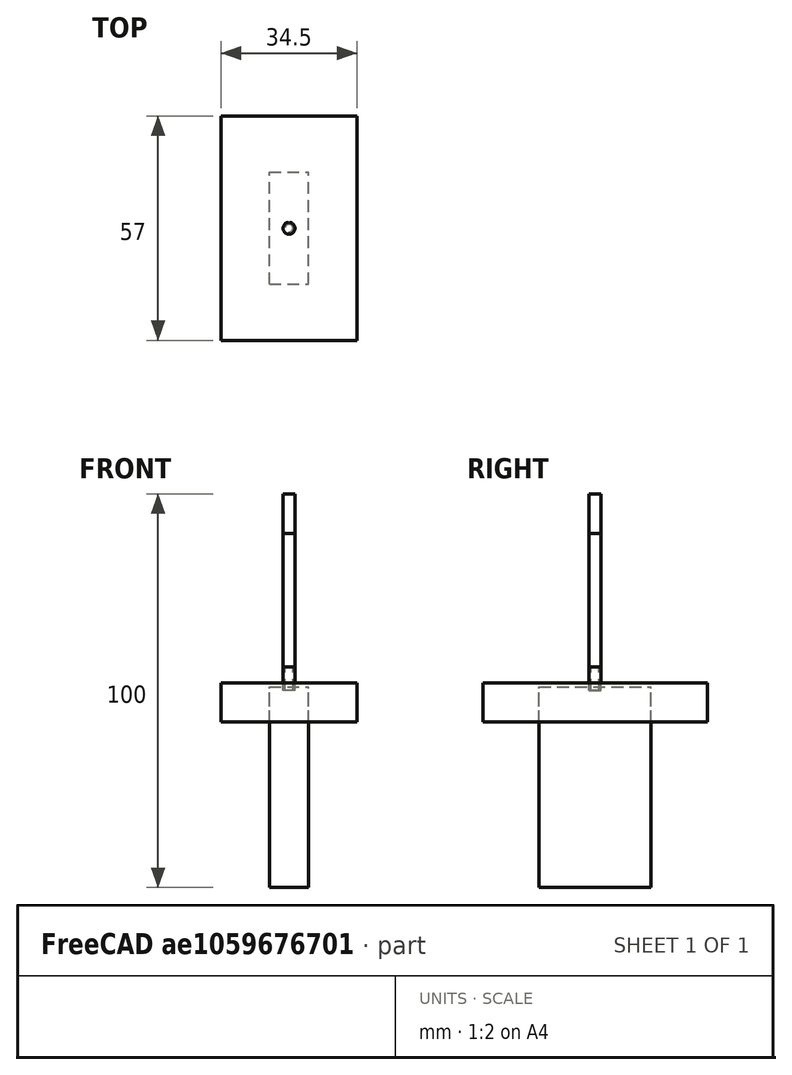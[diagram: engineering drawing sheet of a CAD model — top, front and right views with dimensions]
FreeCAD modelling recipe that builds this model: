
FCSTD DOCUMENT  (FreeCAD 1.0R39109 (Git))
Label: BackFastening_1
License: All rights reserved
LicenseURL: http://en.wikipedia.org/wiki/All_rights_reserved
objects: Path::FeaturePython×15, Part::FeaturePython×11, App::DocumentObjectGroup×9, App::FeaturePython×3, Part::Feature×1
note: 16 computed .brp shape members not serialized (recipe doc carries the construction recipe); baked Part::Feature solids carry a one-line shape summary decoded from their .brp

FEATURE [Part::Feature] Solid  label="PlateFastnest_1"
  shape: bbox 49 x 26.5 x 8 mm, 26 faces (baked)
FEATURE [App::FeaturePython] SetupSheet  # Path/CAM operation (typed FeaturePython)
  ClearanceHeightExpression = OpStockZMax+SetupSheet.ClearanceHeightOffset
  ClearanceHeightOffset = 5
  CoolantMode = 0
  CoolantModes = None | Flood | Mist
  FinalDepthExpression = OpFinalDepth
  HorizRapid = 0
  SafeHeightExpression = OpStockZMax+SetupSheet.SafeHeightOffset
  SafeHeightOffset = 3
  StartDepthExpression = OpStartDepth
  StepDownExpression = OpToolDiameter
  VertRapid = 0
FEATURE [Part::FeaturePython] Clone  label="Model-PlateFastnest_1"  # Draft clone (typed FeaturePython)
  AttacherType = Attacher::AttachEngine3D
  Fuse = false
  Objects = -> [Solid]
  PathResource = Model
  Placement = pos=(-13.25,-24.5,-8) rot=(0,0,-1;4.71239rad)
  Scale = (1,1,1)
FEATURE [App::DocumentObjectGroup] Model
  Group = -> [Clone]
FEATURE [Part::FeaturePython] Stock001  # WARN: FeaturePython — macro-defined, semantics opaque (R4)
  Base = -> Model
  ExtXneg = 4
  ExtXpos = 4
  ExtYneg = 4
  ExtYpos = 4
  ExtZneg = 0
  ExtZpos = 2
  Placement = pos=(-13.25,-24.5,-8) rot=(0,0,1;0rad)
  StockType = FromBase
FEATURE [Part::FeaturePython] ToolBit001  label="3mm Endmill"  # Path/CAM toolbit (typed FeaturePython)
  BitPropertyNames = Chipload | CuttingEdgeHeight | Diameter | Flutes | Length | Material | ShankDiameter | SpindleDirection
  BitShape = <path>
  Chipload = 0
  CuttingEdgeHeight = 15
  Diameter = 3
  File = <path>
  Flutes = 0
  Length = 50
  Material = 0
  ShankDiameter = 3
  ShapeName = endmill
  SpindleDirection = 0
FEATURE [Path::FeaturePython] _mm_Endmill  label="3mm Endmill001"  # Path/CAM operation (typed FeaturePython)
  HorizFeed = 6.66667
  HorizRapid = 0
  SpindleDir = 0
  SpindleSpeed = 10000
  Tool = -> ToolBit001
  ToolNumber = 2
  VertFeed = 6.66667
  VertRapid = 0
  expr: HorizRapid = SetupSheet.HorizRapid
  expr: VertRapid = SetupSheet.VertRapid
FEATURE [App::DocumentObjectGroup] Tools
  Group = -> [_mm_Endmill]
FEATURE [Path::FeaturePython] Adaptive  label="FaceMill"  # Path/CAM operation (typed FeaturePython)
  Active = true
  Base = -> [Clone]
  ClearanceHeight = 7
  CoolantMode = 0
  CycleTime = 00:08:12
  ExtensionCorners = true
  ExtensionFeature = -> [Clone]
  ExtensionLengthDefault = 1.5
  FinalDepth = 0
  FinishDepth = 0
  FinishingProfile = true
  ForceInsideOut = false
  HelixAngle = 5
  HelixConeAngle = 0
  HelixDiameterLimit = 0
  KeepToolDownRatio = 3
  LiftDistance = 0
  OpFinalDepth = 0
  OpStartDepth = 2
  OpStockZMax = 2
  OpStockZMin = -8
  OpToolDiameter = 3
  OperationType = 0
  SafeHeight = 5
  Side = 1
  StartDepth = 2
  StepDown = 3
  StepOver = 20
  StockToLeave = 0
  StopProcessing = false
  Stopped = false
  Tolerance = 0.09
  ToolController = -> _mm_Endmill
  UseHelixArcs = false
  UseOutline = false
  expr: ClearanceHeight = OpStockZMax + SetupSheet.ClearanceHeightOffset
  expr: ExtensionLengthDefault = OpToolDiameter / 2
  expr: FinalDepth = OpFinalDepth
  expr: SafeHeight = OpStockZMax + SetupSheet.SafeHeightOffset
  expr: StartDepth = OpStartDepth
  expr: StepDown = OpToolDiameter
FEATURE [Path::FeaturePython] Adaptive001  label="OutCut"  # Path/CAM operation (typed FeaturePython)
  Active = true
  Base = -> [Clone]
  ClearanceHeight = 7
  CoolantMode = 0
  CycleTime = 00:11:38
  ExtensionCorners = true
  ExtensionLengthDefault = 1.5
  FinalDepth = -8
  FinishDepth = 0
  FinishingProfile = true
  ForceInsideOut = false
  HelixAngle = 5
  HelixConeAngle = 0
  HelixDiameterLimit = 1
  KeepToolDownRatio = 3
  LiftDistance = 0
  OpFinalDepth = -8
  OpStartDepth = 2
  OpStockZMax = 2
  OpStockZMin = -8
  OpToolDiameter = 3
  OperationType = 1
  SafeHeight = 5
  Side = 0
  StartDepth = 2
  StepDown = 6
  StepOver = 20
  StockToLeave = 0
  StopProcessing = false
  Stopped = false
  Tolerance = 0.1
  ToolController = -> _mm_Endmill
  UseHelixArcs = false
  UseOutline = false
  expr: ClearanceHeight = OpStockZMax + SetupSheet.ClearanceHeightOffset
  expr: ExtensionLengthDefault = OpToolDiameter / 2
  expr: FinalDepth = OpFinalDepth
  expr: SafeHeight = OpStockZMax + SetupSheet.SafeHeightOffset
  expr: StartDepth = OpStartDepth
  expr: StepDown = OpToolDiameter * 2
FEATURE [App::DocumentObjectGroup] Operations
  Group = -> [Adaptive,Adaptive001]
FEATURE [Path::FeaturePython] Job  label="OutCut001"  # Path/CAM operation (typed FeaturePython)
  CycleTime = 00:19:50
  Fixtures = G54
  GeometryTolerance = 0.01
  JobType = 0
  Model = -> Model
  Operations = -> Operations
  OrderOutputBy = 0
  PostProcessor = 11
  PostProcessorArgs = --bcnc
  PostProcessorOutputFile = %D\%d_OutCut
  SetupSheet = -> SetupSheet
  SplitOutput = false
  Stock = -> Stock001
  Tools = -> Tools
FEATURE [App::FeaturePython] SetupSheet001  # Path/CAM operation (typed FeaturePython)
  ClearanceHeightExpression = OpStockZMax+SetupSheet001.ClearanceHeightOffset
  ClearanceHeightOffset = 5
  CoolantMode = 0
  CoolantModes = None | Flood | Mist
  FinalDepthExpression = OpFinalDepth
  HorizRapid = 0
  SafeHeightExpression = OpStockZMax+SetupSheet001.SafeHeightOffset
  SafeHeightOffset = 3
  StartDepthExpression = OpStartDepth
  StepDownExpression = OpToolDiameter
  VertRapid = 0
FEATURE [Part::FeaturePython] Clone001  label="Model-Model-PlateFastnest_1"  # Draft clone (typed FeaturePython)
  AttacherType = Attacher::AttachEngine3D
  Fuse = false
  Objects = -> [Clone]
  PathResource = Model
  Placement = pos=(-4,-13.25,-49) rot=(-0.707107,0,-0.707107;3.14159rad)
  Scale = (1,1,1)
FEATURE [App::DocumentObjectGroup] Model001
  Group = -> [Clone001]
FEATURE [Part::FeaturePython] ToolBit002  label="3mm Endmill002"  # Path/CAM toolbit (typed FeaturePython)
  BitPropertyNames = Chipload | CuttingEdgeHeight | Diameter | Flutes | Length | Material | ShankDiameter | SpindleDirection
  BitShape = <path>
  Chipload = 0
  CuttingEdgeHeight = 15
  Diameter = 3
  File = <path>
  Flutes = 0
  Length = 50
  Material = 0
  ShankDiameter = 3
  ShapeName = endmill
  SpindleDirection = 0
FEATURE [Path::FeaturePython] _mm_Endmill002  label="3mm Endmill003"  # Path/CAM operation (typed FeaturePython)
  HorizFeed = 3.33333
  HorizRapid = 0
  SpindleDir = 0
  SpindleSpeed = 10000
  Tool = -> ToolBit002
  ToolNumber = 2
  VertFeed = 3.33333
  VertRapid = 0
  expr: HorizRapid = SetupSheet001.HorizRapid
  expr: VertRapid = SetupSheet001.VertRapid
FEATURE [Path::FeaturePython] Drilling  # Path/CAM operation (typed FeaturePython)
  Active = false
  AddTipLength = false
  Base = -> [Clone001]
  ClearanceHeight = 6
  CoolantMode = 0
  CycleTime = 00:00:22
  DwellEnabled = false
  DwellTime = 1
  ExtraOffset = 0
  FinalDepth = -35
  KeepToolDown = false
  OpFinalDepth = -39
  OpStartDepth = 1
  OpStockZMax = 1
  OpStockZMin = -50
  OpToolDiameter = 3
  PeckDepth = 2.25
  PeckEnabled = true
  RetractHeight = 4
  RetractMode = 0
  SafeHeight = 4
  StartDepth = 1
  ToolController = -> _mm_Endmill002
  chipBreakEnabled = false
  feedRetractEnabled = false
  expr: ClearanceHeight = OpStockZMax + SetupSheet001.ClearanceHeightOffset
  expr: FinalDepth = OpFinalDepth + 4 mm
  expr: PeckDepth = OpToolDiameter * 0.75
  expr: RetractHeight = StartDepth + SetupSheet.SafeHeightOffset
  expr: SafeHeight = OpStockZMax + SetupSheet001.SafeHeightOffset
  expr: StartDepth = OpStartDepth
FEATURE [App::FeaturePython] SetupSheet002  # Path/CAM operation (typed FeaturePython)
  ClearanceHeightExpression = OpStockZMax+SetupSheet002.ClearanceHeightOffset
  ClearanceHeightOffset = 5
  CoolantMode = 0
  CoolantModes = None | Flood | Mist
  FinalDepthExpression = OpFinalDepth
  HorizRapid = 0
  SafeHeightExpression = OpStockZMax+SetupSheet002.SafeHeightOffset
  SafeHeightOffset = 3
  StartDepthExpression = OpStartDepth
  StepDownExpression = OpToolDiameter
  VertRapid = 0
FEATURE [Part::FeaturePython] Clone002  label="Model-Model-PlateFastnest_002"  # Draft clone (typed FeaturePython)
  AttacherType = Attacher::AttachEngine3D
  Fuse = false
  Objects = -> [Clone]
  PathResource = Model
  Placement = pos=(-4,13.25,-3.5e-14) rot=(0,1,0;1.5708rad)
  Scale = (1,1,1)
FEATURE [App::DocumentObjectGroup] Model002
  Group = -> [Clone002]
FEATURE [Part::FeaturePython] ToolBit003  label="3mm Endmill004"  # Path/CAM toolbit (typed FeaturePython)
  BitPropertyNames = Chipload | CuttingEdgeHeight | Diameter | Flutes | Length | Material | ShankDiameter | SpindleDirection
  BitShape = <path>
  Chipload = 0
  CuttingEdgeHeight = 15
  Diameter = 3
  File = <path>
  Flutes = 0
  Length = 50
  Material = 0
  ShankDiameter = 3
  ShapeName = endmill
  SpindleDirection = 0
FEATURE [Path::FeaturePython] _mm_Endmill004  label="3mm Endmill005"  # Path/CAM operation (typed FeaturePython)
  HorizFeed = 6.66667
  HorizRapid = 0
  SpindleDir = 0
  SpindleSpeed = 10000
  Tool = -> ToolBit003
  ToolNumber = 2
  VertFeed = 6.66667
  VertRapid = 0
  expr: HorizRapid = SetupSheet002.HorizRapid
  expr: VertRapid = SetupSheet002.VertRapid
FEATURE [Part::FeaturePython] Stock  # WARN: FeaturePython — macro-defined, semantics opaque (R4)
  Base = -> Model001
  ExtXneg = 1
  ExtXpos = 1
  ExtYneg = 1
  ExtYpos = 1
  ExtZneg = 1
  ExtZpos = 1
  Placement = pos=(-4,-13.25,-49) rot=(0,0,1;0rad)
  StockType = FromBase
FEATURE [Part::FeaturePython] Stock004  # WARN: FeaturePython — macro-defined, semantics opaque (R4)
  Base = -> Model002
  ExtXneg = 1
  ExtXpos = 1
  ExtYneg = 1
  ExtYpos = 1
  ExtZneg = 1
  ExtZpos = 1
  Placement = pos=(-4,-13.25,-49) rot=(0,0,1;0rad)
  StockType = FromBase
FEATURE [Path::FeaturePython] Drilling001  # Path/CAM operation (typed FeaturePython)
  Active = true
  AddTipLength = false
  ClearanceHeight = 0
  CoolantMode = 0
  DwellEnabled = false
  DwellTime = 0
  ExtraOffset = 0
  FinalDepth = 0
  KeepToolDown = false
  OpFinalDepth = 0
  OpStartDepth = 0
  OpStockZMax = 0
  OpStockZMin = 0
  OpToolDiameter = 0
  PeckDepth = 0
  PeckEnabled = false
  RetractHeight = 0
  RetractMode = 0
  SafeHeight = 0
  StartDepth = 0
  chipBreakEnabled = false
  feedRetractEnabled = false
FEATURE [Path::FeaturePython] Drilling002  # Path/CAM operation (typed FeaturePython)
  Active = false
  AddTipLength = false
  Base = -> [Clone002]
  ClearanceHeight = 6
  CoolantMode = 0
  CycleTime = 00:00:06
  DwellEnabled = false
  DwellTime = 1
  ExtraOffset = 0
  FinalDepth = -6
  KeepToolDown = false
  OpFinalDepth = -10
  OpStartDepth = 1
  OpStockZMax = 1
  OpStockZMin = -50
  OpToolDiameter = 3
  PeckDepth = 0.75
  PeckEnabled = true
  RetractHeight = 4
  RetractMode = 0
  SafeHeight = 4
  StartDepth = 1
  ToolController = -> _mm_Endmill004
  chipBreakEnabled = false
  feedRetractEnabled = false
  expr: ClearanceHeight = OpStockZMax + SetupSheet002.ClearanceHeightOffset
  expr: FinalDepth = OpFinalDepth + 4 mm
  expr: PeckDepth = OpToolDiameter * 0.25
  expr: RetractHeight = StartDepth + SetupSheet.SafeHeightOffset
  expr: SafeHeight = OpStockZMax + SetupSheet002.SafeHeightOffset
  expr: StartDepth = OpStartDepth
FEATURE [Part::FeaturePython] ToolBit  label="2mm Endmill"  # Path/CAM toolbit (typed FeaturePython)
  BitPropertyNames = Chipload | CuttingEdgeHeight | Diameter | Flutes | Length | Material | ShankDiameter | SpindleDirection
  BitShape = <path>
  Chipload = 0
  CuttingEdgeHeight = 6
  Diameter = 2
  File = <userpath>/Desktop/CNC/ToolBit/Bit/2mm_Endmill.fctb
  Flutes = 0
  Length = 40
  Material = 0
  ShankDiameter = 3
  ShapeName = endmill
  SpindleDirection = 0
FEATURE [Path::FeaturePython] _mm_Endmill005  label="2mm Endmill001"  # Path/CAM operation (typed FeaturePython)
  HorizFeed = 3.33333
  HorizRapid = 0
  SpindleDir = 0
  SpindleSpeed = 10000
  Tool = -> ToolBit
  ToolNumber = 3
  VertFeed = 3.33333
  VertRapid = 0
  expr: HorizRapid = SetupSheet001.HorizRapid
  expr: VertRapid = SetupSheet001.VertRapid
FEATURE [App::DocumentObjectGroup] Tools001
  Group = -> [_mm_Endmill002,_mm_Endmill005]
FEATURE [Path::FeaturePython] Adaptive002  # Path/CAM operation (typed FeaturePython)
  Active = true
  Base = -> [Clone001]
  ClearanceHeight = 6
  CoolantMode = 0
  CycleTime = 00:03:35
  ExtensionCorners = true
  ExtensionLengthDefault = 1
  FinalDepth = -10
  FinishDepth = 0
  FinishingProfile = true
  ForceInsideOut = false
  HelixAngle = 5
  HelixConeAngle = 0
  HelixDiameterLimit = 0.25
  KeepToolDownRatio = 3
  LiftDistance = 0
  OpFinalDepth = -10
  OpStartDepth = 1
  OpStockZMax = 1
  OpStockZMin = -50
  OpToolDiameter = 2
  OperationType = 0
  SafeHeight = 4
  Side = 1
  StartDepth = 1
  StepDown = 2
  StepOver = 10
  StockToLeave = 0
  StopProcessing = false
  Stopped = false
  Tolerance = 0.1
  ToolController = -> _mm_Endmill005
  UseHelixArcs = false
  UseOutline = false
  expr: ClearanceHeight = OpStockZMax + SetupSheet001.ClearanceHeightOffset
  expr: ExtensionLengthDefault = OpToolDiameter / 2
  expr: FinalDepth = OpFinalDepth
  expr: SafeHeight = OpStockZMax + SetupSheet001.SafeHeightOffset
  expr: StartDepth = OpStartDepth
  expr: StepDown = OpToolDiameter
FEATURE [App::DocumentObjectGroup] Operations001
  Group = -> [Drilling,Adaptive002]
FEATURE [Path::FeaturePython] Job001  label="Side1"  # Path/CAM operation (typed FeaturePython)
  CycleTime = 00:03:35
  Fixtures = G54
  GeometryTolerance = 0.01
  JobType = 0
  Model = -> Model001
  Operations = -> Operations001
  OrderOutputBy = 0
  PostProcessor = 11
  PostProcessorArgs = --bcnc
  PostProcessorOutputFile = %D\%d_side1
  SetupSheet = -> SetupSheet001
  SplitOutput = false
  Stock = -> Stock
  Tools = -> Tools001
FEATURE [Part::FeaturePython] ToolBit004  label="2mm Endmill002"  # Path/CAM toolbit (typed FeaturePython)
  BitPropertyNames = Chipload | CuttingEdgeHeight | Diameter | Flutes | Length | Material | ShankDiameter | SpindleDirection
  BitShape = <path>
  Chipload = 0
  CuttingEdgeHeight = 6
  Diameter = 2
  File = <userpath>/Desktop/CNC/ToolBit/Bit/2mm_Endmill.fctb
  Flutes = 0
  Length = 40
  Material = 0
  ShankDiameter = 3
  ShapeName = endmill
  SpindleDirection = 0
FEATURE [Path::FeaturePython] _mm_Endmill006  label="2mm Endmill003"  # Path/CAM operation (typed FeaturePython)
  HorizFeed = 3.33333
  HorizRapid = 0
  SpindleDir = 0
  SpindleSpeed = 10000
  Tool = -> ToolBit004
  ToolNumber = 3
  VertFeed = 3.33333
  VertRapid = 0
  expr: HorizRapid = SetupSheet002.HorizRapid
  expr: VertRapid = SetupSheet002.VertRapid
FEATURE [App::DocumentObjectGroup] Tools002
  Group = -> [_mm_Endmill004,_mm_Endmill006]
FEATURE [Path::FeaturePython] Adaptive003  # Path/CAM operation (typed FeaturePython)
  Active = true
  Base = -> [Clone002]
  ClearanceHeight = 6
  CoolantMode = 0
  CycleTime = 00:01:40
  ExtensionCorners = true
  ExtensionLengthDefault = 1
  FinalDepth = -4
  FinishDepth = 0
  FinishingProfile = true
  ForceInsideOut = false
  HelixAngle = 5
  HelixConeAngle = 0
  HelixDiameterLimit = 0.25
  KeepToolDownRatio = 3
  LiftDistance = 0
  OpFinalDepth = -10
  OpStartDepth = 1
  OpStockZMax = 1
  OpStockZMin = -50
  OpToolDiameter = 2
  OperationType = 0
  SafeHeight = 4
  Side = 1
  StartDepth = 1
  StepDown = 2
  StepOver = 20
  StockToLeave = 0
  StopProcessing = false
  Stopped = false
  Tolerance = 0.1
  ToolController = -> _mm_Endmill006
  UseHelixArcs = false
  UseOutline = false
  expr: ClearanceHeight = OpStockZMax + SetupSheet002.ClearanceHeightOffset
  expr: ExtensionLengthDefault = OpToolDiameter / 2
  expr: FinalDepth = OpFinalDepth + 6 mm
  expr: SafeHeight = OpStockZMax + SetupSheet002.SafeHeightOffset
  expr: StartDepth = OpStartDepth
  expr: StepDown = OpToolDiameter
FEATURE [App::DocumentObjectGroup] Operations002
  Group = -> [Drilling002,Adaptive003]
FEATURE [Path::FeaturePython] Job002  label="Side2"  # Path/CAM operation (typed FeaturePython)
  CycleTime = 00:01:40
  Fixtures = G54
  GeometryTolerance = 0.01
  JobType = 0
  Model = -> Model002
  Operations = -> Operations002
  OrderOutputBy = 0
  PostProcessor = 11
  PostProcessorArgs = --bcnc
  PostProcessorOutputFile = %D\%d_side2
  SetupSheet = -> SetupSheet002
  SplitOutput = false
  Stock = -> Stock004
  Tools = -> Tools002
note: 8 file-system paths scrubbed to <path> (originals preserved in the JSON sidecar)
